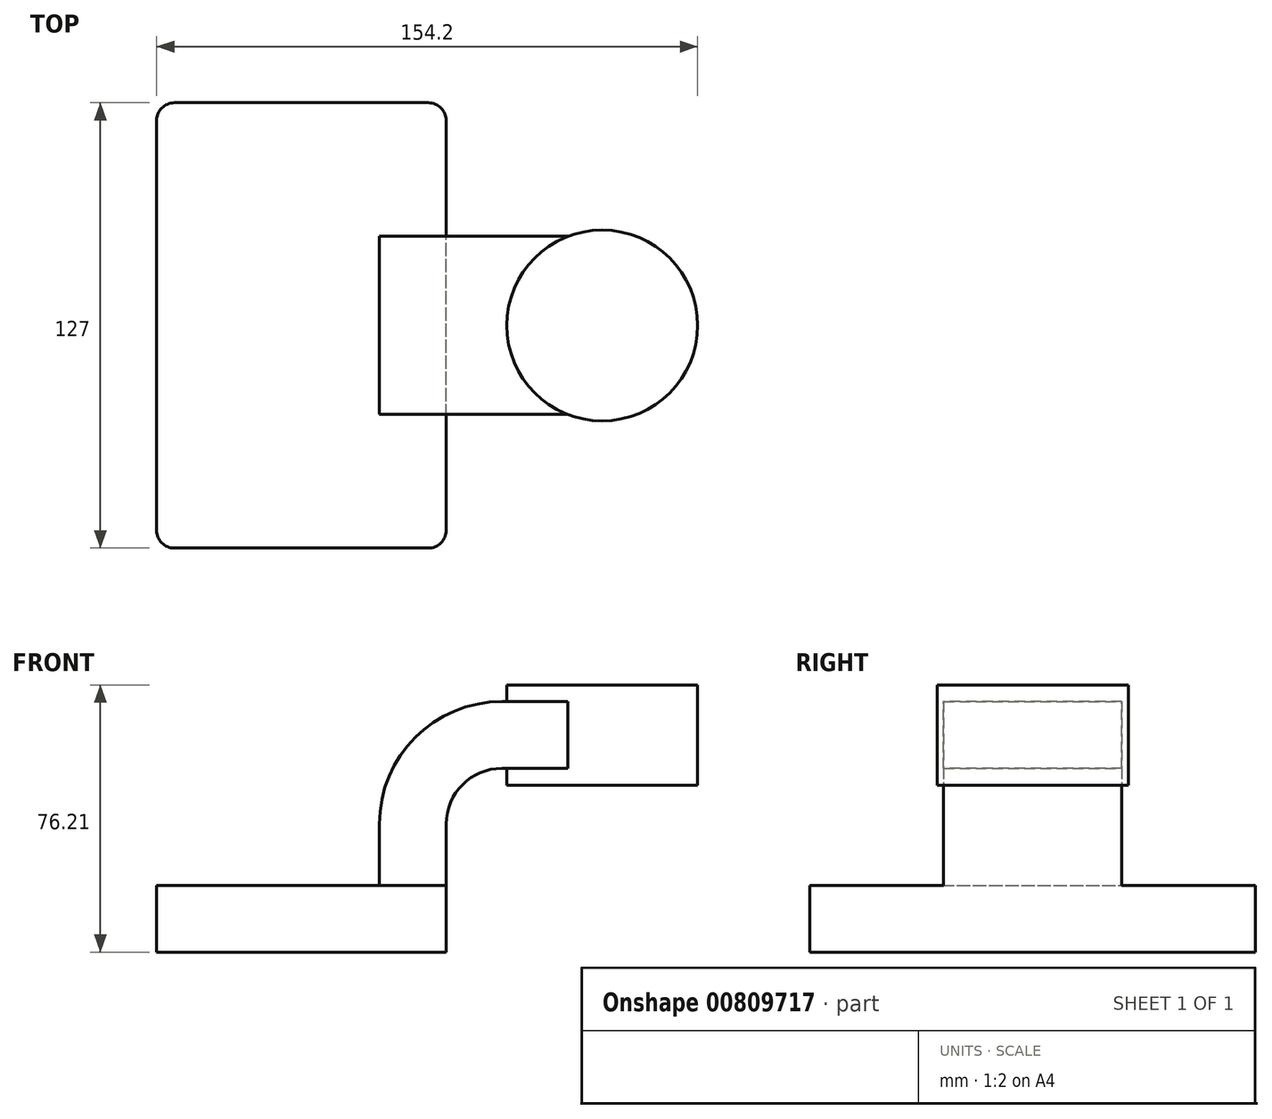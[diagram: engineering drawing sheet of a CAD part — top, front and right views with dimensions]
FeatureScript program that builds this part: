
annotation { "Feature Type Name" : "Feature", "Feature Type Description" : "" }
export const myFeature = defineFeature(function(context is Context, id is Id, definition is map)
    precondition{}
    {
        {
            var Q0;
            Q0=qCreatedBy(makeId("Front.planeOp"),FACE);
            var sketch = newSketch(context, id + "F0", { "sketchPlane" : qUnion([Q0])});
            skLineSegment(sketch, "E0.bottom", {"start": v(-41.28, -9.53) * mm, "end": v(41.28, -9.53) * mm});
            skLineSegment(sketch, "E0.top", {"start": v(-41.28, 9.53) * mm, "end": v(41.28, 9.53) * mm});
            skLineSegment(sketch, "E0.left", {"start": v(-41.28, -9.53) * mm, "end": v(-41.28, 9.53) * mm});
            skLineSegment(sketch, "E0.right", {"start": v(41.28, -9.53) * mm, "end": v(41.28, 9.53) * mm});
            skPoint(sketch, "E0.middle", {"position": v(0, 0) * mm});
            skLineSegment(sketch, "E1.bottom", {"start": v(62.13, 38.1) * mm, "end": v(112.93, 38.1) * mm});
            skLineSegment(sketch, "E1.top", {"start": v(62.13, 66.67) * mm, "end": v(112.93, 66.67) * mm});
            skLineSegment(sketch, "E1.left", {"start": v(62.13, 38.1) * mm, "end": v(62.13, 66.67) * mm});
            skLineSegment(sketch, "E1.right", {"start": v(112.93, 38.1) * mm, "end": v(112.93, 66.67) * mm});
            skPoint(sketch, "E1.middle", {"position": v(87.53, 52.39) * mm});
            skLineSegment(sketch, "E2", {"start": v(41.27, 9.53) * mm, "end": v(41.27, 27) * mm});
            skArc(sketch, "E3", {"start": v(41.27, 27) * mm, "mid": v(45.92, 38.23) * mm, "end": v(57.15, 42.88) * mm});
            skLineSegment(sketch, "E4", {"start": v(57.15, 42.88) * mm, "end": v(85.72, 42.88) * mm});
            skLineSegment(sketch, "E5.0", {"start": v(57.15, 61.93) * mm, "end": v(85.72, 61.93) * mm});
            skArc(sketch, "E5.1", {"start": v(22.23, 27) * mm, "mid": v(32.45, 51.7) * mm, "end": v(57.15, 61.93) * mm});
            skLineSegment(sketch, "E5.2", {"start": v(22.22, 9.53) * mm, "end": v(22.22, 27) * mm});
            skLineSegment(sketch, "E6", {"start": v(85.72, 61.93) * mm, "end": v(85.72, 42.88) * mm});
            skFitSpline(sketch, "E7", {"points": [v(-41.28, 9.53) * mm, v(57.15, 61.93) * mm], "startDerivative": vector(51.19, 78.54) * mm, "endDerivative": vector(157.09, -7.52) * mm});
            skLineSegment(sketch, "E8", {"start": v(85.72, 42.88) * mm, "end": v(85.72, 38.1) * mm});
            skLineSegment(sketch, "E9", {"start": v(85.72, 61.93) * mm, "end": v(85.72, 66.67) * mm});
            skSolve(sketch);
        }
        {
            var Q0;
            Q0=makeQuery(id+"F0.imprint","IMPRINT",FACE,{"disambiguationData":[TD([[makeQuery(id+"F0.imprint","IMPRINT",EDGE,{"derivedFrom":sQuery(id+"F0.wireOp",EDGE,"E0.bottom")}),1.0]])]});
            extrude(context, id + "F1", {"entities" : qUnion([Q0]), "endBound" : BoundingType.SYMMETRIC, "depth" : 127 * mm, "offsetDistance" : 25.4 * mm});
        }
        {
            var Q0;
            {var subQ0=sQuery(id+"F0.wireOp",EDGE,"E2");Q0=makeQuery(id+"F0.imprint","IMPRINT",FACE,{"disambiguationData":[TD([[makeQuery(id+"F0.imprint","IMPRINT",EDGE,{"derivedFrom":subQ0}),1.0]])]});}
            var Q1;
            {var subQ5=sQuery(id+"F0.wireOp",EDGE,"E6");Q1=makeQuery(id+"F0.imprint","IMPRINT",FACE,{"disambiguationData":[TD([[makeQuery(id+"F0.imprint","IMPRINT",EDGE,{"derivedFrom":subQ5}),-1.0]])]});}
            extrude(context, id + "F2", {"entities" : qUnion([Q0, Q1]), "operationType" : NewBodyOperationType.ADD, "endBound" : BoundingType.SYMMETRIC, "depth" : 50.8 * mm, "offsetDistance" : 25.4 * mm});
        }
        {
            var Q0;
            Q0=makeQuery(id+"F0.imprint","IMPRINT",FACE,{"disambiguationData":[TD([[makeQuery(id+"F0.imprint","IMPRINT",EDGE,{"derivedFrom":sQuery(id+"F0.wireOp",EDGE,"E5.1")}),1.0]])]});
            extrude(context, id + "F3", {"entities" : qUnion([Q0]), "operationType" : NewBodyOperationType.ADD, "endBound" : BoundingType.SYMMETRIC, "depth" : 25.4 * mm, "offsetDistance" : 25.4 * mm});
        }
        {
            var Q0;
            {var subQ0=sQuery(id+"F0.wireOp",EDGE,"E1.right");Q0=makeQuery(id+"F0.imprint","IMPRINT",FACE,{"disambiguationData":[TD([[makeQuery(id+"F0.imprint","IMPRINT",EDGE,{"derivedFrom":subQ0}),1.0]])]});}
            var Q1;
            Q1=sQuery(id+"F0.wireOp",EDGE,"E6");
            revolve(context, id + "F4", {"operationType" : NewBodyOperationType.ADD, "surfaceOperationType" : NewSurfaceOperationType.NEW, "entities" : qUnion([Q0]), "axis" : qUnion([Q1]), "revolveType" : RevolveType.FULL});
        }
        {
            var Q0;
            Q0=makeQuery(id+"F1.opExtrude","CAP_EDGE",EDGE,{"disambiguationData":[OSD([sQuery(id+"F0.wireOp",EDGE,"E0.right")])],"isStart":false});
            var Q1;
            Q1=makeQuery(id+"F2.opExtrude","CAP_EDGE",EDGE,{"disambiguationData":[OSD([sQuery(id+"F0.wireOp",EDGE,"E0.top")])],"isStart":false});
            var Q2;
            Q2=makeQuery(id+"F3.opExtrude","CAP_EDGE",EDGE,{"disambiguationData":[OSD([sQuery(id+"F0.wireOp",EDGE,"E0.top")])],"isStart":false});
            var Q3;
            {var subQ0=sQuery(id+"F0.wireOp",EDGE,"E0.top");var subQ1=sQuery(id+"F0.wireOp",EDGE,"E5.2");var subQ2=sQuery(id+"F0.wireOp",EDGE,"E5.1");Q3=makeQuery(id+"F3.boolean.opBoolean","SPLIT",EDGE,{"disambiguationData":[TD([makeQuery(id+"F3.opExtrude","CAP_FACE",FACE,{"disambiguationData":[OSD([subQ0,subQ2,subQ1,sQuery(id+"F0.wireOp",EDGE,"E7")])],"isStart":false})])],"derivedFrom":makeQuery(id+"F2.opExtrude","SWEPT_EDGE",EDGE,{"disambiguationData":[OSD([subQ0,subQ1])]})});}
            var Q4;
            Q4=makeQuery(id+"F3.opExtrude","CAP_EDGE",EDGE,{"disambiguationData":[OSD([sQuery(id+"F0.wireOp",EDGE,"E5.2")])],"isStart":false});
            var Q5;
            Q5=makeQuery(id+"F3.opExtrude","CAP_EDGE",EDGE,{"disambiguationData":[OSD([sQuery(id+"F0.wireOp",EDGE,"E5.1")])],"isStart":true});
            var Q6;
            Q6=makeQuery(id+"F3.opExtrude","CAP_EDGE",EDGE,{"disambiguationData":[OSD([sQuery(id+"F0.wireOp",EDGE,"E0.top")])],"isStart":true});
            var Q7;
            {var subQ0=sQuery(id+"F0.wireOp",EDGE,"E0.top");var subQ1=sQuery(id+"F0.wireOp",EDGE,"E5.2");var subQ2=sQuery(id+"F0.wireOp",EDGE,"E5.1");Q7=makeQuery(id+"F3.boolean.opBoolean","SPLIT",EDGE,{"disambiguationData":[TD([makeQuery(id+"F3.opExtrude","CAP_FACE",FACE,{"disambiguationData":[OSD([subQ0,subQ2,subQ1,sQuery(id+"F0.wireOp",EDGE,"E7")])],"isStart":true})])],"derivedFrom":makeQuery(id+"F2.opExtrude","SWEPT_EDGE",EDGE,{"disambiguationData":[OSD([subQ0,subQ1])]})});}
            var Q8;
            Q8=makeQuery(id+"F1.opExtrude","CAP_EDGE",EDGE,{"disambiguationData":[OSD([sQuery(id+"F0.wireOp",EDGE,"E0.left")])],"isStart":true});
            var Q9;
            Q9=makeQuery(id+"F1.opExtrude","CAP_EDGE",EDGE,{"disambiguationData":[OSD([sQuery(id+"F0.wireOp",EDGE,"E0.right")])],"isStart":true});
            fillet(context, id + "F5", {"entities" : qUnion([Q0, Q1, Q2, Q3, Q4, Q5, Q6, Q7, Q8, Q9]), "radius" : 5.08 * mm, "tangentPropagation" : true, "allowEdgeOverflow" : false});
        }
        {
            var Q0;
            Q0=makeQuery(id+"F1.opExtrude","CAP_EDGE",EDGE,{"disambiguationData":[OSD([sQuery(id+"F0.wireOp",EDGE,"E0.left")])],"isStart":false});
            fillet(context, id + "F6", {"entities" : qUnion([Q0]), "radius" : 5.08 * mm, "tangentPropagation" : true, "allowEdgeOverflow" : false});
        }
    });
